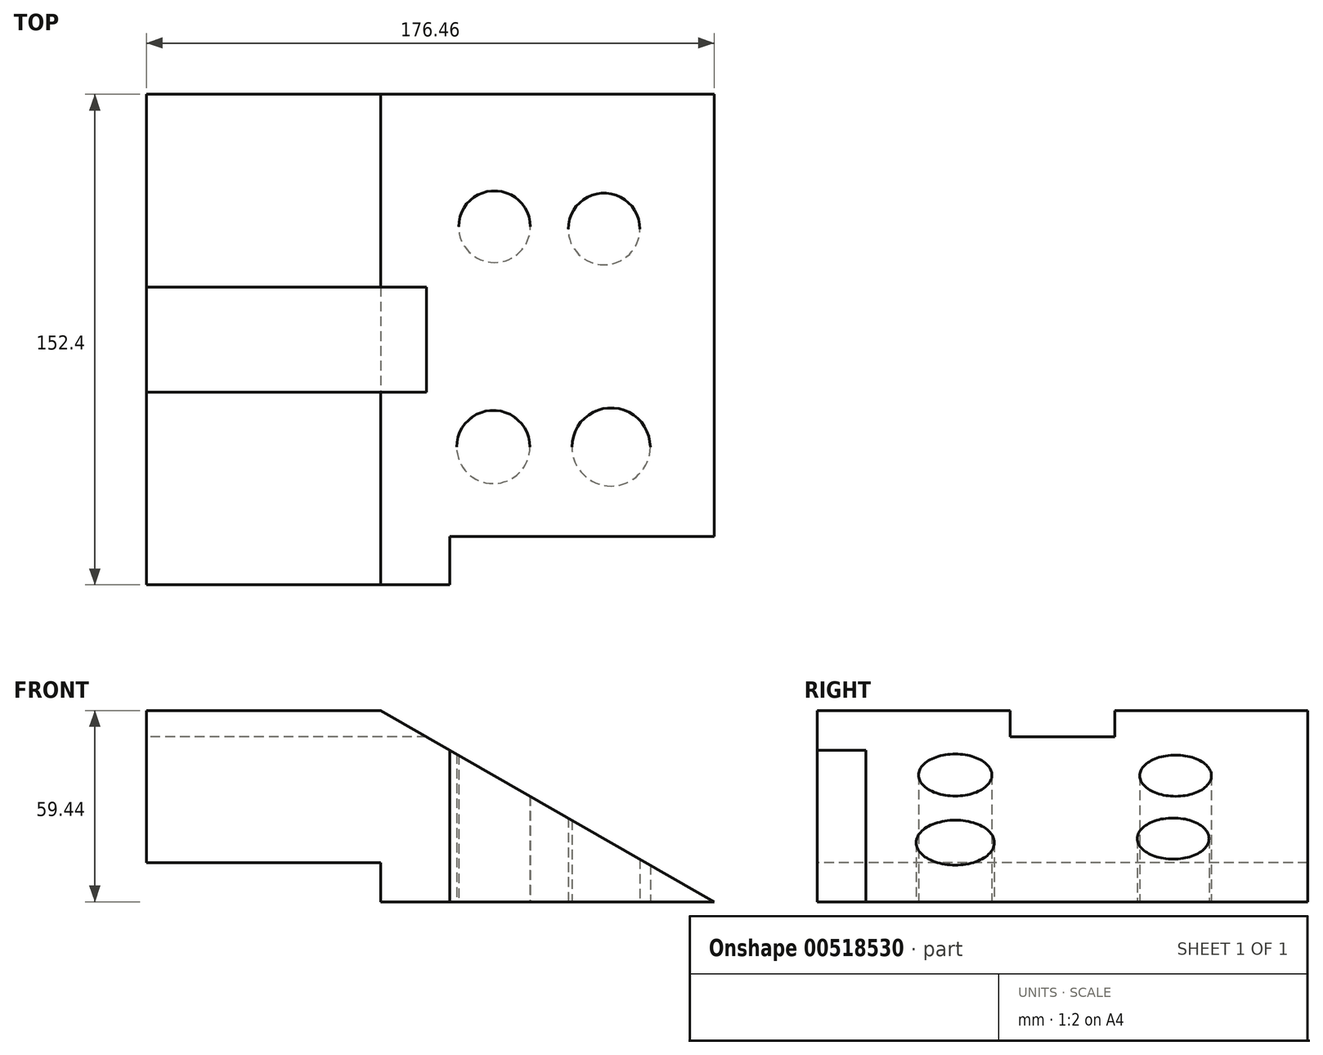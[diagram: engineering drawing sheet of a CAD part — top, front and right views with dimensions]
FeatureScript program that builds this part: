
annotation { "Feature Type Name" : "Feature", "Feature Type Description" : "" }
export const myFeature = defineFeature(function(context is Context, id is Id, definition is map)
    precondition{}
    {
        {
            var Q0;
            Q0=qCreatedBy(makeId("Front.planeOp"),FACE);
            var sketch = newSketch(context, id + "F0", { "sketchPlane" : qUnion([Q0])});
            skLineSegment(sketch, "E0", {"start": v(0, 37.12) * mm, "end": v(103.61, -22.32) * mm});
            skLineSegment(sketch, "E1", {"start": v(103.61, -22.32) * mm, "end": v(-72.85, -22.32) * mm});
            skLineSegment(sketch, "E2", {"start": v(-72.85, -22.32) * mm, "end": v(-72.85, 37.12) * mm});
            skLineSegment(sketch, "E3", {"start": v(-72.85, 37.12) * mm, "end": v(0, 37.12) * mm});
            skSolve(sketch);
        }
        {
            var Q0;
            Q0 = qSketchRegion(id + "F0", true);
            extrude(context, id + "F1", {"entities" : qUnion([Q0]), "depth" : 76.2 * mm, "offsetDistance" : 25.4 * mm});
        }
        {
            var Q0;
            Q0=makeQuery(id+"F1.opExtrude","CAP_FACE",FACE,{"disambiguationData":[OSD([sQuery(id+"F0.wireOp",EDGE,"E0"),sQuery(id+"F0.wireOp",EDGE,"E1"),sQuery(id+"F0.wireOp",EDGE,"E2"),sQuery(id+"F0.wireOp",EDGE,"E3")])],"isStart":true});
            extrude(context, id + "F2", {"entities" : qUnion([Q0]), "operationType" : NewBodyOperationType.ADD, "depth" : 76.2 * mm, "offsetDistance" : 25.4 * mm});
        }
        {
            var Q0;
            Q0=makeQuery(id+"F1.opExtrude","CAP_FACE",FACE,{"disambiguationData":[OSD([sQuery(id+"F0.wireOp",EDGE,"E0"),sQuery(id+"F0.wireOp",EDGE,"E1"),sQuery(id+"F0.wireOp",EDGE,"E2"),sQuery(id+"F0.wireOp",EDGE,"E3")])],"isStart":false});
            var sketch = newSketch(context, id + "F3", { "sketchPlane" : qUnion([Q0])});
            skLineSegment(sketch, "E4.bottom", {"start": v(-72.85, -22.32) * mm, "end": v(0, -22.32) * mm});
            skLineSegment(sketch, "E4.top", {"start": v(-72.85, -10.22) * mm, "end": v(0, -10.22) * mm});
            skLineSegment(sketch, "E4.left", {"start": v(-72.85, -22.32) * mm, "end": v(-72.85, -10.22) * mm});
            skLineSegment(sketch, "E4.right", {"start": v(0, -22.32) * mm, "end": v(0, -10.22) * mm});
            skSolve(sketch);
        }
        {
            var Q0;
            Q0=makeQuery(id+"F3.imprint","IMPRINT",FACE,{"disambiguationData":[TD([[makeQuery(id+"F3.imprint","IMPRINT",EDGE,{"derivedFrom":sQuery(id+"F3.wireOp",EDGE,"E4.bottom")}),-1.0]])]});
            extrude(context, id + "F4", {"entities" : qUnion([Q0]), "operationType" : NewBodyOperationType.REMOVE, "endBound" : BoundingType.THROUGH_ALL, "oppositeDirection" : true, "depth" : 25.4 * mm, "offsetDistance" : 25.4 * mm});
        }
        {
            var Q0;
            {var subQ0=sQuery(id+"F0.wireOp",EDGE,"E1");Q0=makeQuery(id+"F2.boolean.opBoolean","MERGE",FACE,{"derivedFrom":[makeQuery(id+"F1.opExtrude","SWEPT_FACE",FACE,{"disambiguationData":[OSD([subQ0])]}),makeQuery(id+"F2.opExtrude","SWEPT_FACE",FACE,{"disambiguationData":[OSD([subQ0])]})]});}
            var sketch = newSketch(context, id + "F5", { "sketchPlane" : qUnion([Q0])});
            skLineSegment(sketch, "E5.bottom", {"start": v(21.5, 76.2) * mm, "end": v(103.61, 76.2) * mm});
            skLineSegment(sketch, "E5.top", {"start": v(21.5, 61.09) * mm, "end": v(103.61, 61.09) * mm});
            skLineSegment(sketch, "E5.left", {"start": v(21.5, 76.2) * mm, "end": v(21.5, 61.09) * mm});
            skLineSegment(sketch, "E5.right", {"start": v(103.61, 76.2) * mm, "end": v(103.61, 61.09) * mm});
            skSolve(sketch);
        }
        {
            var Q0;
            Q0 = qSketchRegion(id + "F5", true);
            extrude(context, id + "F6", {"entities" : qUnion([Q0]), "operationType" : NewBodyOperationType.REMOVE, "endBound" : BoundingType.THROUGH_ALL, "oppositeDirection" : true, "depth" : 25.4 * mm, "offsetDistance" : 25.4 * mm});
        }
        {
            var Q0;
            {var subQ0=sQuery(id+"F0.wireOp",EDGE,"E2");Q0=makeQuery(id+"F2.boolean.opBoolean","MERGE",FACE,{"derivedFrom":[makeQuery(id+"F1.opExtrude","SWEPT_FACE",FACE,{"disambiguationData":[OSD([subQ0])]}),makeQuery(id+"F2.opExtrude","SWEPT_FACE",FACE,{"disambiguationData":[OSD([subQ0])]})]});}
            var sketch = newSketch(context, id + "F7", { "sketchPlane" : qUnion([Q0])});
            skLineSegment(sketch, "E6.bottom", {"start": v(16.29, 37.12) * mm, "end": v(-16.29, 37.12) * mm});
            skLineSegment(sketch, "E6.top", {"start": v(16.29, 28.95) * mm, "end": v(-16.29, 28.95) * mm});
            skLineSegment(sketch, "E6.left", {"start": v(16.29, 37.12) * mm, "end": v(16.29, 28.95) * mm});
            skLineSegment(sketch, "E6.right", {"start": v(-16.29, 37.12) * mm, "end": v(-16.29, 28.95) * mm});
            skPoint(sketch, "E6.middle", {"position": v(0, 33.03) * mm});
            skSolve(sketch);
        }
        {
            var Q0;
            Q0 = qSketchRegion(id + "F7", true);
            extrude(context, id + "F8", {"entities" : qUnion([Q0]), "operationType" : NewBodyOperationType.REMOVE, "endBound" : BoundingType.THROUGH_ALL, "oppositeDirection" : true, "depth" : 25.4 * mm, "offsetDistance" : 25.4 * mm});
        }
        {
            var Q0;
            {var subQ0=sQuery(id+"F0.wireOp",EDGE,"E1");Q0=makeQuery(id+"F2.boolean.opBoolean","MERGE",FACE,{"derivedFrom":[makeQuery(id+"F1.opExtrude","SWEPT_FACE",FACE,{"disambiguationData":[OSD([subQ0])]}),makeQuery(id+"F2.opExtrude","SWEPT_FACE",FACE,{"disambiguationData":[OSD([subQ0])]})]});}
            var sketch = newSketch(context, id + "F9", { "sketchPlane" : qUnion([Q0])});
            skCircle(sketch, "E7", {"center": v(34.97, 33.3) * mm, "radius": 11.4 * mm});
            skSolve(sketch);
        }
        {
            var Q0;
            Q0 = qSketchRegion(id + "F9", true);
            extrude(context, id + "F10", {"entities" : qUnion([Q0]), "operationType" : NewBodyOperationType.REMOVE, "endBound" : BoundingType.THROUGH_ALL, "oppositeDirection" : true, "depth" : 25.4 * mm, "offsetDistance" : 25.4 * mm});
        }
        {
            var Q0;
            {var subQ0=sQuery(id+"F0.wireOp",EDGE,"E1");Q0=makeQuery(id+"F2.boolean.opBoolean","MERGE",FACE,{"derivedFrom":[makeQuery(id+"F1.opExtrude","SWEPT_FACE",FACE,{"disambiguationData":[OSD([subQ0])]}),makeQuery(id+"F2.opExtrude","SWEPT_FACE",FACE,{"disambiguationData":[OSD([subQ0])]})]});}
            var sketch = newSketch(context, id + "F11", { "sketchPlane" : qUnion([Q0])});
            skCircle(sketch, "E8", {"center": v(71.57, 33.3) * mm, "radius": 12.17 * mm});
            skSolve(sketch);
        }
        {
            var Q0;
            Q0 = qSketchRegion(id + "F11", true);
            extrude(context, id + "F12", {"entities" : qUnion([Q0]), "operationType" : NewBodyOperationType.REMOVE, "endBound" : BoundingType.THROUGH_ALL, "oppositeDirection" : true, "depth" : 25.4 * mm, "offsetDistance" : 25.4 * mm});
        }
        {
            var Q0;
            {var subQ0=sQuery(id+"F0.wireOp",EDGE,"E1");Q0=makeQuery(id+"F2.boolean.opBoolean","MERGE",FACE,{"derivedFrom":[makeQuery(id+"F1.opExtrude","SWEPT_FACE",FACE,{"disambiguationData":[OSD([subQ0])]}),makeQuery(id+"F2.opExtrude","SWEPT_FACE",FACE,{"disambiguationData":[OSD([subQ0])]})]});}
            var sketch = newSketch(context, id + "F13", { "sketchPlane" : qUnion([Q0])});
            skCircle(sketch, "E9", {"center": v(35.34, -35.14) * mm, "radius": 11.16 * mm});
            skSolve(sketch);
        }
        {
            var Q0;
            Q0 = qSketchRegion(id + "F13", true);
            extrude(context, id + "F14", {"entities" : qUnion([Q0]), "operationType" : NewBodyOperationType.REMOVE, "endBound" : BoundingType.THROUGH_ALL, "oppositeDirection" : true, "depth" : 25.4 * mm, "offsetDistance" : 25.4 * mm});
        }
        {
            var Q0;
            {var subQ0=sQuery(id+"F0.wireOp",EDGE,"E1");Q0=makeQuery(id+"F2.boolean.opBoolean","MERGE",FACE,{"derivedFrom":[makeQuery(id+"F1.opExtrude","SWEPT_FACE",FACE,{"disambiguationData":[OSD([subQ0])]}),makeQuery(id+"F2.opExtrude","SWEPT_FACE",FACE,{"disambiguationData":[OSD([subQ0])]})]});}
            var sketch = newSketch(context, id + "F15", { "sketchPlane" : qUnion([Q0])});
            skCircle(sketch, "E10", {"center": v(69.38, -34.4) * mm, "radius": 11.16 * mm});
            skSolve(sketch);
        }
        {
            var Q0;
            Q0 = qSketchRegion(id + "F15", true);
            extrude(context, id + "F16", {"entities" : qUnion([Q0]), "operationType" : NewBodyOperationType.REMOVE, "endBound" : BoundingType.THROUGH_ALL, "oppositeDirection" : true, "depth" : 25.4 * mm, "offsetDistance" : 25.4 * mm});
        }
    });
